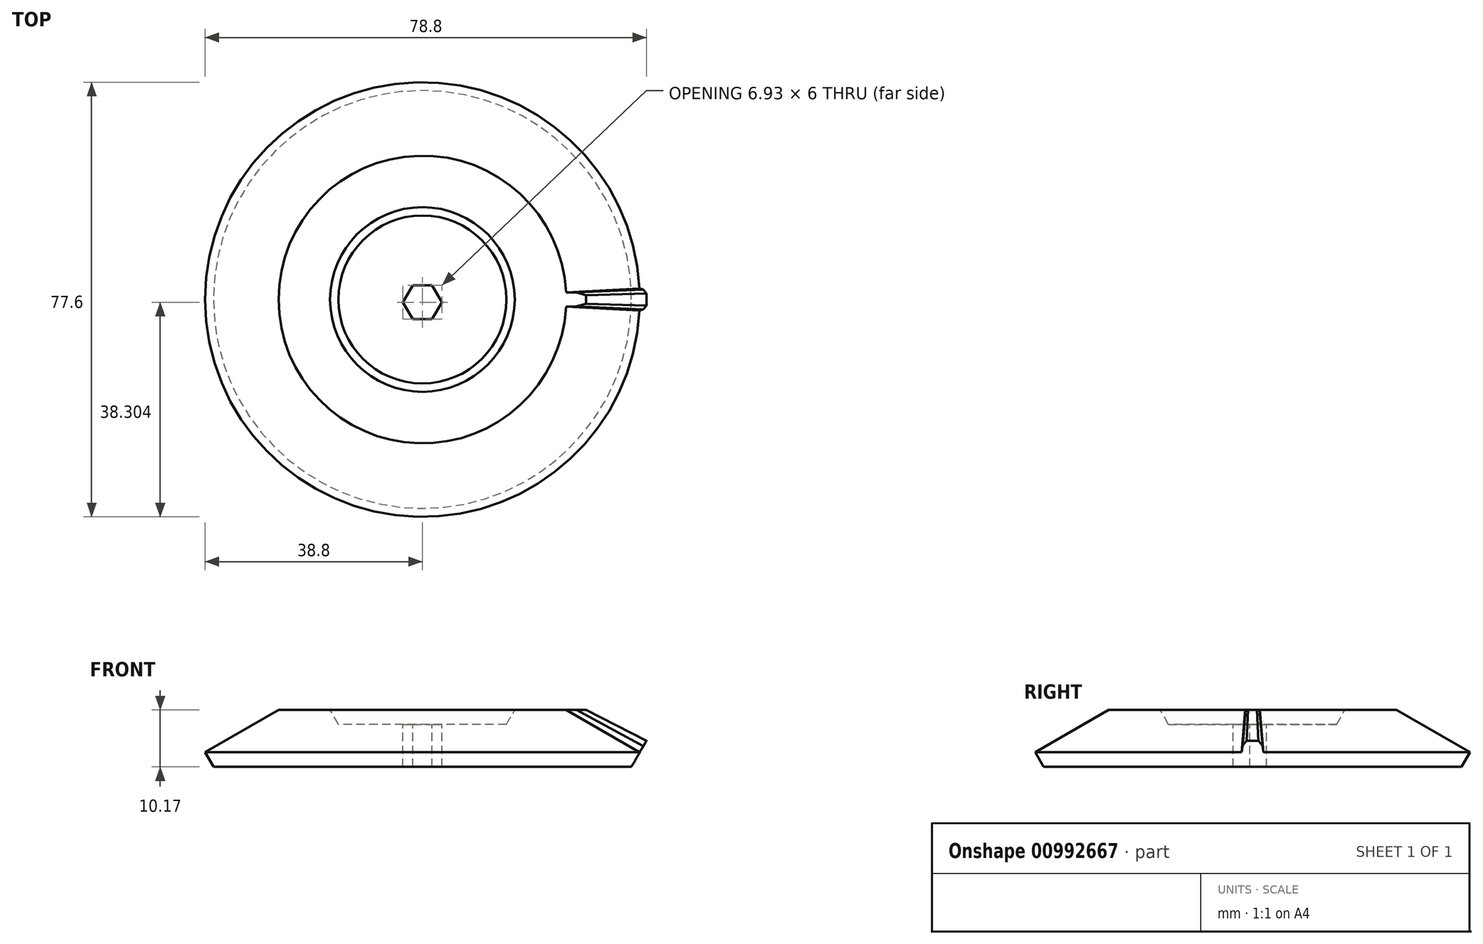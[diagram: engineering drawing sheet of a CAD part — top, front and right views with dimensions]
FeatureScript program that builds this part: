
annotation { "Feature Type Name" : "Feature", "Feature Type Description" : "" }
export const myFeature = defineFeature(function(context is Context, id is Id, definition is map)
    precondition{}
    {
        {
            var Q0;
            Q0=qCreatedBy(makeId("Front.planeOp"),FACE);
            var sketch = newSketch(context, id + "F0", { "sketchPlane" : qUnion([Q0])});
            skLineSegment(sketch, "E0", {"start": v(0, 0) * mm, "end": v(37.3, 0) * mm});
            skLineSegment(sketch, "E1", {"start": v(38.8, 2.6) * mm, "end": v(0, 25) * mm});
            skLineSegment(sketch, "E2", {"start": v(37.3, 0) * mm, "end": v(38.8, 2.6) * mm});
            skLineSegment(sketch, "E3", {"start": v(37.3, 0) * mm, "end": v(43.3, 0) * mm, "construction": true});
            skLineSegment(sketch, "E4", {"start": v(43.3, 0) * mm, "end": v(38.8, 2.6) * mm, "construction": true});
            skLineSegment(sketch, "E5", {"start": v(0, 25) * mm, "end": v(0, 0) * mm});
            skSolve(sketch);
        }
        {
            var Q0;
            Q0 = qSketchRegion(id + "F0", true);
            var Q1;
            Q1=sQuery(id+"F0.wireOp",EDGE,"E5");
            revolve(context, id + "F1", {"surfaceOperationType" : NewSurfaceOperationType.NEW, "entities" : qUnion([Q0]), "axis" : qUnion([Q1]), "revolveType" : RevolveType.FULL});
        }
        {
            var Q0;
            Q0=sQuery(id+"F0.wireOp",EDGE,"E1");
            var Q1;
            Q1=sQuery(id+"F0.wireOp",VERTEX,"E1.start");
            cPlane(context, id + "F2", {"entities" : qUnion([Q0, Q1]), "cplaneType" : CPlaneType.LINE_POINT, "offset" : 25 * mm, "width" : 150 * mm, "height" : 150 * mm});
        }
        {
            var Q0;
            Q0=qCreatedBy(id+"F2.planeOp",FACE);
            var sketch = newSketch(context, id + "F3", { "sketchPlane" : qUnion([Q0])});
            skPoint(sketch, "E6.0", {"position": v(0, 21.65) * mm});
            skLineSegment(sketch, "E7", {"start": v(0, 21.65) * mm, "end": v(0, 21.3) * mm, "construction": true});
            skLineSegment(sketch, "E8", {"start": v(0, 21.3) * mm, "end": v(-2, 21.3) * mm, "construction": true});
            skLineSegment(sketch, "E9", {"start": v(-2, 21.3) * mm, "end": v(-1.96, 21.63) * mm, "construction": true});
            skLineSegment(sketch, "E10", {"start": v(-1.78, 22.94) * mm, "end": v(-1.08, 24.05) * mm});
            skLineSegment(sketch, "E11", {"start": v(-1.08, 24.05) * mm, "end": v(0, 24.05) * mm});
            skLineSegment(sketch, "E12", {"start": v(0, 24.05) * mm, "end": v(0, 21.65) * mm, "construction": true});
            skLineSegment(sketch, "E13.MirrorCS", {"start": v(0, 21.3) * mm, "end": v(2, 21.3) * mm, "construction": true});
            skLineSegment(sketch, "E14.MirrorCS", {"start": v(2, 21.3) * mm, "end": v(1.96, 21.63) * mm, "construction": true});
            skLineSegment(sketch, "E15.MirrorCS", {"start": v(1.78, 22.94) * mm, "end": v(1.08, 24.05) * mm});
            skLineSegment(sketch, "E16.MirrorCS", {"start": v(1.08, 24.05) * mm, "end": v(0, 24.05) * mm});
            skEllipticalArc(sketch, "E17.0", {});
            skLineSegment(sketch, "E18", {"start": v(1.96, 21.63) * mm, "end": v(1.78, 22.94) * mm});
            skLineSegment(sketch, "E19", {"start": v(-1.96, 21.63) * mm, "end": v(-1.78, 22.94) * mm});
            const initialGuessF3  = {"E17.0": [0, 0.00225, 1, 0, 0.0388, 0.0194, 1.5203313466643227, 1.6212613069254707]};
            skSetInitialGuess(sketch, initialGuessF3);
            skSolve(sketch);
        }
        {
            var Q1;
            Q1=sQuery(id+"F0.wireOp",VERTEX,"E1.end");
            var Q2;
            Q2=makeQuery(id+"F3.imprint","IMPRINT",FACE,{"disambiguationData":[TD([[makeQuery(id+"F3.imprint","IMPRINT",EDGE,{"derivedFrom":sQuery(id+"F3.wireOp",EDGE,"E10")}),-1.0]])]});
            loft(context, id + "F4", {"operationType" : NewBodyOperationType.ADD, "sheetProfilesArray" : [{ "sheetProfileEntities" : qUnion([Q1]) }, { "sheetProfileEntities" : qUnion([Q2]) }]});
        }
        {
            var Q0;
            Q0=qCreatedBy(makeId("Front.planeOp"),FACE);
            var sketch = newSketch(context, id + "F5", { "sketchPlane" : qUnion([Q0])});
            skPoint(sketch, "E20.0", {"position": v(0, 25) * mm});
            skLineSegment(sketch, "E21", {"start": v(0, 25) * mm, "end": v(38.8, 2.6) * mm, "construction": true});
            skLineSegment(sketch, "E22", {"start": v(16.49, 10.17) * mm, "end": v(15, 7.6) * mm});
            skLineSegment(sketch, "E23", {"start": v(15, 7.6) * mm, "end": v(0, 7.6) * mm});
            skLineSegment(sketch, "E24", {"start": v(0, 7.6) * mm, "end": v(0, 34.04) * mm});
            skLineSegment(sketch, "E25", {"start": v(16.49, 10.17) * mm, "end": v(36, 10.17) * mm});
            skLineSegment(sketch, "E26", {"start": v(36, 10.17) * mm, "end": v(41.44, 7.18) * mm});
            skLineSegment(sketch, "E27", {"start": v(44.39, 2.6) * mm, "end": v(44.39, 8.97) * mm});
            skLineSegment(sketch, "E28", {"start": v(44.39, 8.97) * mm, "end": v(0, 34.04) * mm});
            skLineSegment(sketch, "E29", {"start": v(41.44, 7.18) * mm, "end": v(37.3, 0) * mm});
            skPoint(sketch, "E30.0", {"position": v(37.3, 0) * mm});
            skLineSegment(sketch, "E31", {"start": v(37.3, 0) * mm, "end": v(44.39, 2.6) * mm});
            skPoint(sketch, "E32", {"position": v(25.68, 10.17) * mm});
            skSolve(sketch);
        }
        {
            var Q0;
            Q0=makeQuery(id+"F5.imprint","IMPRINT",FACE,{"disambiguationData":[TD([[makeQuery(id+"F5.imprint","IMPRINT",EDGE,{"derivedFrom":sQuery(id+"F5.wireOp",EDGE,"E22")}),-1.0]])]});
            var Q1;
            Q1=sQuery(id+"F5.wireOp",EDGE,"E24");
            revolve(context, id + "F6", {"operationType" : NewBodyOperationType.REMOVE, "surfaceOperationType" : NewSurfaceOperationType.NEW, "entities" : qUnion([Q0]), "axis" : qUnion([Q1]), "revolveType" : RevolveType.FULL, "oppositeDirection" : true});
        }
        {
            var Q0;
            Q0=makeQuery(id+"F6.boolean.opBoolean","COPY",FACE,{"derivedFrom":makeQuery(id+"F6.opRevolve","SWEPT_FACE",FACE,{"disambiguationData":[OSD([sQuery(id+"F5.wireOp",EDGE,"E23")])]})});
            var sketch = newSketch(context, id + "F7", { "sketchPlane" : qUnion([Q0])});
            skCircle(sketch, "E33.cCircle", {"center": v(0, -0.5) * mm, "radius": 3 * mm, "construction": true});
            skLineSegment(sketch, "E33.0", {"start": v(-1.73, 2.5) * mm, "end": v(1.73, 2.5) * mm});
            skLineSegment(sketch, "E33.1", {"start": v(1.73, 2.5) * mm, "end": v(3.46, -0.5) * mm});
            skLineSegment(sketch, "E33.2", {"start": v(3.46, -0.5) * mm, "end": v(1.73, -3.5) * mm});
            skLineSegment(sketch, "E33.3", {"start": v(1.73, -3.5) * mm, "end": v(-1.73, -3.5) * mm});
            skLineSegment(sketch, "E33.4", {"start": v(-1.73, -3.5) * mm, "end": v(-3.46, -0.5) * mm});
            skLineSegment(sketch, "E33.5", {"start": v(-3.46, -0.5) * mm, "end": v(-1.73, 2.5) * mm});
            skPoint(sketch, "E33.0.midPoint", {"position": v(0, 2.5) * mm});
            skSolve(sketch);
        }
        {
            var Q0;
            Q0=makeQuery(id+"F7.imprint","IMPRINT",FACE,{"disambiguationData":[TD([[makeQuery(id+"F7.imprint","IMPRINT",EDGE,{"derivedFrom":sQuery(id+"F7.wireOp",EDGE,"E33.0")}),-1.0]])]});
            extrude(context, id + "F8", {"entities" : qUnion([Q0]), "operationType" : NewBodyOperationType.REMOVE, "endBound" : BoundingType.THROUGH_ALL, "oppositeDirection" : true, "depth" : 25 * mm, "offsetDistance" : 25 * mm});
        }
    });
